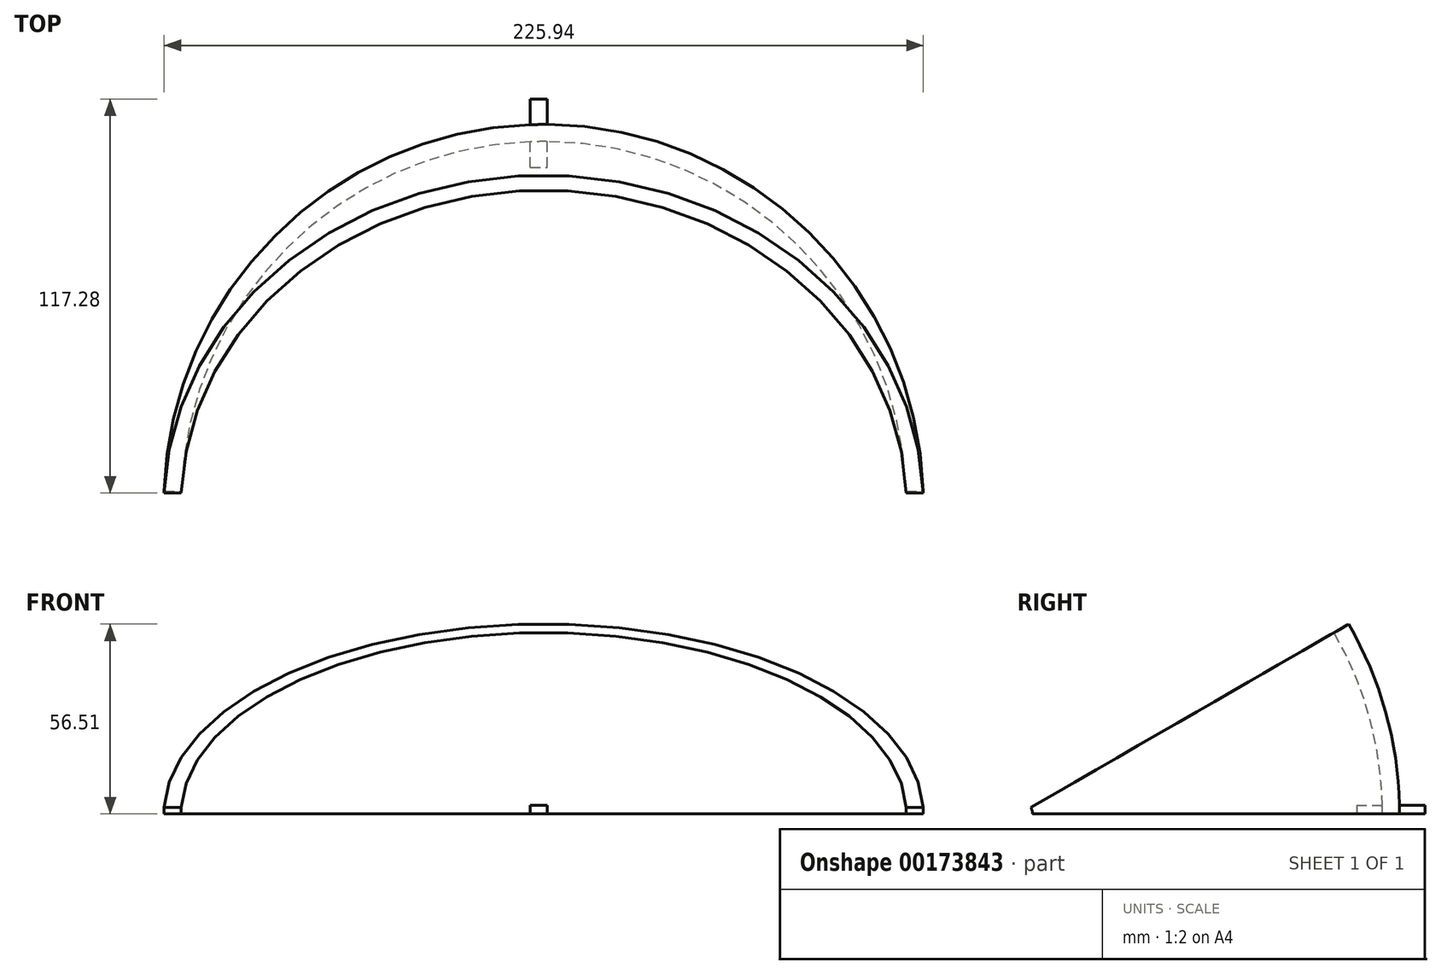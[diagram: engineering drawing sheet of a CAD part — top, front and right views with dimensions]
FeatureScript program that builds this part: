
annotation { "Feature Type Name" : "Feature", "Feature Type Description" : "" }
export const myFeature = defineFeature(function(context is Context, id is Id, definition is map)
    precondition{}
    {
        {
            var Q0;
            Q0=qCreatedBy(makeId("Top.planeOp"),FACE);
            var sketch = newSketch(context, id + "F0", { "sketchPlane" : qUnion([Q0])});
            skLineSegment(sketch, "E0", {"start": v(0, 0) * mm, "end": v(-107.95, 0) * mm, "construction": true});
            skArc(sketch, "E1", {"start": v(-107.95, 0) * mm, "mid": v(0, 107.95) * mm, "end": v(107.95, 0) * mm});
            skLineSegment(sketch, "E2", {"start": v(-107.95, 0) * mm, "end": v(-113.03, 0) * mm});
            skArc(sketch, "E3", {"start": v(-113.03, 0) * mm, "mid": v(0, 113.03) * mm, "end": v(113.03, 0) * mm});
            skLineSegment(sketch, "E4", {"start": v(107.95, 0) * mm, "end": v(113.03, 0) * mm});
            skSolve(sketch);
        }
        {
            var Q0;
            Q0=qSketchRegion(id+"F0",true);
            var Q1;
            Q1=sQuery(id+"F0.wireOp",EDGE,"E0");
            revolve(context, id + "F1", {"entities" : qUnion([Q0]), "axis" : qUnion([Q1]), "revolveType" : RevolveType.ONE_DIRECTION, "oppositeDirection" : true, "angle" : 30 * degree});
        }
        {
            var Q0;
            Q0=qCreatedBy(makeId("Right.planeOp"),FACE);
            var sketch = newSketch(context, id + "F2", { "sketchPlane" : qUnion([Q0])});
            skCircle(sketch, "E5", {"center": v(0, 0) * mm, "radius": 3.81 * mm});
            skSolve(sketch);
        }
        {
            var Q0;
            Q0=qSketchRegion(id+"F2",true);
            extrude(context, id + "F3", {"entities" : qUnion([Q0]), "operationType" : NewBodyOperationType.REMOVE, "endBound" : BoundingType.THROUGH_ALL, "oppositeDirection" : true, "depth" : 25.4 * mm, "hasSecondDirection" : true, "secondDirectionBound" : SecondDirectionBoundingType.THROUGH_ALL, "secondDirectionOppositeDirection" : false, "secondDirectionDepth" : 25.4 * mm});
        }
        {
            var Q0;
            Q0=qCreatedBy(makeId("Top.planeOp"),FACE);
            var sketch = newSketch(context, id + "F4", { "sketchPlane" : qUnion([Q0])});
            skLineSegment(sketch, "E6", {"start": v(0, 0) * mm, "end": v(2.54, 0) * mm, "construction": true});
            skLineSegment(sketch, "E7", {"start": v(0, 0) * mm, "end": v(-2.54, 0) * mm, "construction": true});
            skLineSegment(sketch, "E8", {"start": v(0, 0) * mm, "end": v(-107.95, 0) * mm, "construction": true});
            skLineSegment(sketch, "E9", {"start": v(0, 0) * mm, "end": v(-113.03, 0) * mm, "construction": true});
            skArc(sketch, "E10", {"start": v(-113.03, 0) * mm, "mid": v(0, 113.03) * mm, "end": v(113.03, 0) * mm, "construction": true});
            skLineSegment(sketch, "E11", {"start": v(-4.04, 112.96) * mm, "end": v(-4.04, 120.58) * mm, "construction": true});
            skLineSegment(sketch, "E12", {"start": v(-4.04, 120.58) * mm, "end": v(1.04, 120.58) * mm});
            skArc(sketch, "E13", {"start": v(-107.95, 0) * mm, "mid": v(0, 107.95) * mm, "end": v(107.95, 0) * mm, "construction": true});
            skLineSegment(sketch, "E14", {"start": v(-4.04, 107.87) * mm, "end": v(-4.04, 100.25) * mm, "construction": true});
            skLineSegment(sketch, "E15.bottom", {"start": v(-4.04, 100.25) * mm, "end": v(1.04, 100.25) * mm});
            skLineSegment(sketch, "E15.left", {"start": v(-4.04, 100.25) * mm, "end": v(-4.04, 120.58) * mm});
            skLineSegment(sketch, "E15.right", {"start": v(1.04, 100.25) * mm, "end": v(1.04, 120.58) * mm});
            skLineSegment(sketch, "E16", {"start": v(-4.04, 100.25) * mm, "end": v(-2.54, 0) * mm, "construction": true});
            skLineSegment(sketch, "E17", {"start": v(2.54, 0) * mm, "end": v(1.04, 107.95) * mm, "construction": true});
            skSolve(sketch);
        }
        {
            var Q0;
            Q0 = qSketchRegion(id + "F4", true);
            extrude(context, id + "F5", {"entities" : qUnion([Q0]), "operationType" : NewBodyOperationType.ADD, "depth" : 2.54 * mm});
        }
    });
